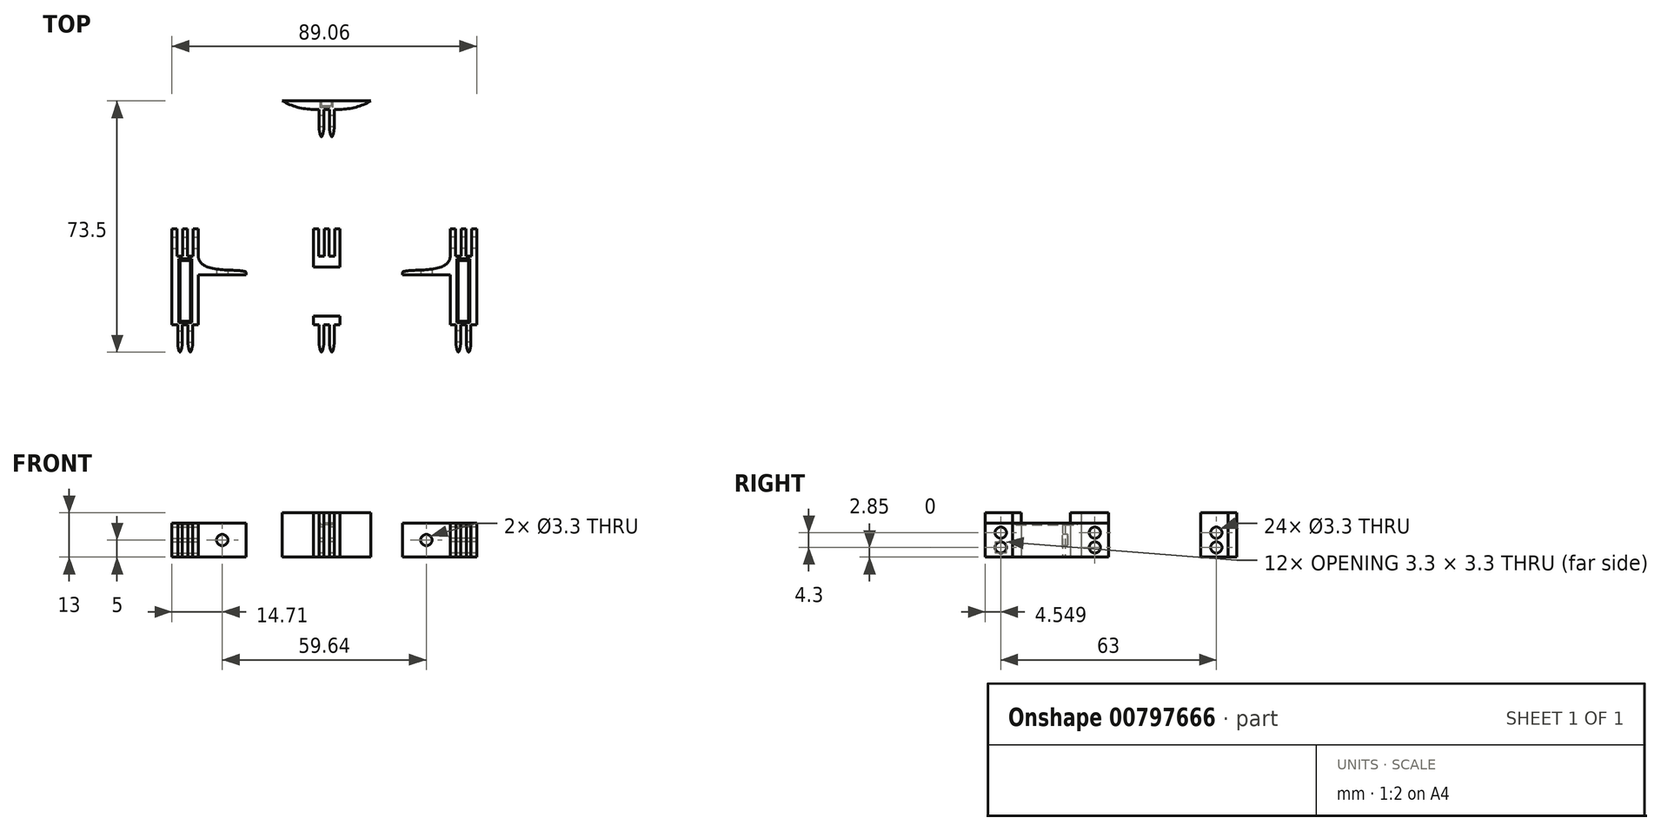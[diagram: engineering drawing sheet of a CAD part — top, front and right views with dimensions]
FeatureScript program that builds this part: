
annotation { "Feature Type Name" : "Feature", "Feature Type Description" : "" }
export const myFeature = defineFeature(function(context is Context, id is Id, definition is map)
    precondition{}
    {
        {
            var Q0;
            Q0=qCreatedBy(makeId("Top.planeOp"),FACE);
            var sketch = newSketch(context, id + "F0", { "sketchPlane" : qUnion([Q0])});
            skLineSegment(sketch, "E0", {"start": v(-17.18, 0) * mm, "end": v(-3.18, 0) * mm});
            skLineSegment(sketch, "E1", {"start": v(-3.18, 0) * mm, "end": v(-3.18, 11.16) * mm});
            skLineSegment(sketch, "E2", {"start": v(4.53, 11.16) * mm, "end": v(4.53, -16.94) * mm});
            skLineSegment(sketch, "E3", {"start": v(-17.18, 0) * mm, "end": v(-17.18, -2.3) * mm});
            skLineSegment(sketch, "E4", {"start": v(-17.18, -2.3) * mm, "end": v(-3.18, -2.3) * mm});
            skLineSegment(sketch, "E5", {"start": v(-3.18, -2.3) * mm, "end": v(-3.18, -16.94) * mm});
            skLineSegment(sketch, "E6", {"start": v(-3.18, 11.16) * mm, "end": v(-1.68, 11.16) * mm});
            skLineSegment(sketch, "E7", {"start": v(3.03, 11.16) * mm, "end": v(4.53, 11.16) * mm});
            skLineSegment(sketch, "E8", {"start": v(-1.68, 11.16) * mm, "end": v(-1.68, 3.06) * mm});
            skLineSegment(sketch, "E9", {"start": v(-1.68, 3.06) * mm, "end": v(0, 3.06) * mm});
            skLineSegment(sketch, "E10", {"start": v(0, 3.06) * mm, "end": v(0, 11.16) * mm});
            skLineSegment(sketch, "E11", {"start": v(0, 11.16) * mm, "end": v(1.35, 11.16) * mm});
            skLineSegment(sketch, "E12", {"start": v(1.35, 11.16) * mm, "end": v(1.35, 3.06) * mm});
            skLineSegment(sketch, "E13", {"start": v(1.35, 3.06) * mm, "end": v(3.03, 3.06) * mm});
            skLineSegment(sketch, "E14", {"start": v(3.03, 3.06) * mm, "end": v(3.03, 11.16) * mm});
            skLineSegment(sketch, "E15", {"start": v(4.53, -16.94) * mm, "end": v(2.86, -16.94) * mm});
            skLineSegment(sketch, "E16", {"start": v(2.86, -16.94) * mm, "end": v(2.86, -24.94) * mm});
            skLineSegment(sketch, "E17", {"start": v(2.86, -24.94) * mm, "end": v(1.51, -24.94) * mm});
            skLineSegment(sketch, "E18", {"start": v(1.52, -24.94) * mm, "end": v(1.52, -16.94) * mm});
            skLineSegment(sketch, "E19", {"start": v(1.51, -16.94) * mm, "end": v(-0.17, -16.94) * mm});
            skLineSegment(sketch, "E20", {"start": v(-0.17, -16.94) * mm, "end": v(-0.17, -24.94) * mm});
            skLineSegment(sketch, "E21", {"start": v(-0.17, -24.94) * mm, "end": v(-1.51, -24.94) * mm});
            skLineSegment(sketch, "E22", {"start": v(-1.51, -24.94) * mm, "end": v(-1.51, -16.94) * mm});
            skLineSegment(sketch, "E23", {"start": v(-1.51, -16.94) * mm, "end": v(-3.18, -16.94) * mm});
            skPoint(sketch, "E24", {"position": v(-10.18, -2.3) * mm});
            skLineSegment(sketch, "E25", {"start": v(-3.18, -14.44) * mm, "end": v(4.53, -14.44) * mm});
            skLineSegment(sketch, "E26", {"start": v(4.53, -14.44) * mm, "end": v(13.62, -14.44) * mm});
            skArc(sketch, "E27", {"start": v(4.53, -16.94) * mm, "mid": v(9.24, -16.28) * mm, "end": v(13.62, -14.44) * mm});
            skPoint(sketch, "E28", {"position": v(0.67, -14.44) * mm});
            skLineSegment(sketch, "E29", {"start": v(0.67, -14.44) * mm, "end": v(0.67, -16.3) * mm, "construction": true});
            skLineSegment(sketch, "E30.MirrorCS", {"start": v(-3.18, -14.44) * mm, "end": v(-12.27, -14.44) * mm});
            skArc(sketch, "E31.MirrorCS", {"start": v(-3.18, -16.94) * mm, "mid": v(-7.89, -16.28) * mm, "end": v(-12.27, -14.44) * mm});
            skLineSegment(sketch, "E32", {"start": v(-17.18, -2.3) * mm, "end": v(-17.18, -1.53) * mm});
            skFitSpline(sketch, "E33", {"points": [v(-17.18, -1.53) * mm, v(-3.18, 3.24) * mm], "startDerivative": vector(5.77, 3.68) * mm, "endDerivative": vector(0, 16.63) * mm});
            skLineSegment(sketch, "E34", {"start": v(-1.98, -16.94) * mm, "end": v(-1.98, -19.6) * mm, "construction": true});
            skLineSegment(sketch, "E35", {"start": v(-1.98, -19.6) * mm, "end": v(-1.98, -22.27) * mm, "construction": true});
            skLineSegment(sketch, "E36", {"start": v(-1.98, -22.27) * mm, "end": v(-1.98, -24.94) * mm, "construction": true});
            skPoint(sketch, "E37", {"position": v(-1.51, -22.44) * mm});
            skPoint(sketch, "E38", {"position": v(-0.17, -22.44) * mm});
            skFitSpline(sketch, "E39", {"points": [v(-1.51, -22.44) * mm, v(-0.84, -24.94) * mm, v(-0.17, -22.44) * mm], "startDerivative": vector(0, -3.73) * mm, "endDerivative": vector(0, 3.73) * mm});
            skLineSegment(sketch, "E40", {"start": v(0.67, -16.94) * mm, "end": v(0.67, -25.95) * mm, "construction": true});
            skFitSpline(sketch, "E41.MirrorCS", {"points": [v(2.86, -22.44) * mm, v(2.19, -24.94) * mm, v(1.52, -22.44) * mm], "startDerivative": vector(0, -3.73) * mm, "endDerivative": vector(0, 3.73) * mm});
            skLineSegment(sketch, "E42", {"start": v(-3.18, 0) * mm, "end": v(4.53, 0) * mm});
            skSolve(sketch);
        }
        {
            var Q0;
            {var subQ0=sQuery(id+"F0.wireOp",EDGE,"E0");Q0=makeQuery(id+"F0.imprint","IMPRINT",FACE,{"disambiguationData":[TD([[makeQuery(id+"F0.imprint","IMPRINT",EDGE,{"derivedFrom":subQ0}),1.0]])]});}
            var Q1;
            {var subQ7=sQuery(id+"F0.wireOp",EDGE,"E4");Q1=makeQuery(id+"F0.imprint","IMPRINT",FACE,{"disambiguationData":[TD([[makeQuery(id+"F0.imprint","IMPRINT",EDGE,{"derivedFrom":subQ7}),1.0]])]});}
            var Q2;
            {var subQ0=sQuery(id+"F0.wireOp",EDGE,"E15");Q2=makeQuery(id+"F0.imprint","IMPRINT",FACE,{"disambiguationData":[TD([[makeQuery(id+"F0.imprint","IMPRINT",EDGE,{"derivedFrom":subQ0}),-1.0]])]});}
            var Q3;
            {var subQ4=sQuery(id+"F0.wireOp",EDGE,"E6");Q3=makeQuery(id+"F0.imprint","IMPRINT",FACE,{"disambiguationData":[TD([[makeQuery(id+"F0.imprint","IMPRINT",EDGE,{"derivedFrom":subQ4}),-1.0]])]});}
            extrude(context, id + "F1", {"entities" : qUnion([Q0, Q1, Q2, Q3]), "depth" : 10 * mm, "offsetDistance" : 25 * mm});
        }
        {
            var Q0;
            {var subQ2=sQuery(id+"F0.wireOp",EDGE,"E30.MirrorCS");Q0=makeQuery(id+"F0.imprint","IMPRINT",FACE,{"disambiguationData":[TD([[makeQuery(id+"F0.imprint","IMPRINT",EDGE,{"derivedFrom":subQ2}),1.0]])]});}
            var Q1;
            {var subQ0=sQuery(id+"F0.wireOp",EDGE,"E15");Q1=makeQuery(id+"F0.imprint","IMPRINT",FACE,{"disambiguationData":[TD([[makeQuery(id+"F0.imprint","IMPRINT",EDGE,{"derivedFrom":subQ0}),-1.0]])]});}
            var Q2;
            {var subQ2=sQuery(id+"F0.wireOp",EDGE,"E26");Q2=makeQuery(id+"F0.imprint","IMPRINT",FACE,{"disambiguationData":[TD([[makeQuery(id+"F0.imprint","IMPRINT",EDGE,{"derivedFrom":subQ2}),-1.0]])]});}
            extrude(context, id + "F2", {"entities" : qUnion([Q0, Q1, Q2]), "depth" : 13 * mm, "offsetDistance" : 25 * mm});
        }
        {
            var Q0;
            Q0=makeQuery(id+"F1.opExtrude","SWEPT_FACE",FACE,{"disambiguationData":[OSD([sQuery(id+"F0.wireOp",EDGE,"E4")])]});
            var sketch = newSketch(context, id + "F3", { "sketchPlane" : qUnion([Q0])});
            skLineSegment(sketch, "E43.0", {"start": v(-17.18, 0) * mm, "end": v(-3.18, 0) * mm});
            skLineSegment(sketch, "E44.0", {"start": v(-17.18, 10) * mm, "end": v(-3.18, 10) * mm});
            skLineSegment(sketch, "E45", {"start": v(-3.18, 10) * mm, "end": v(-17.18, 0) * mm});
            skLineSegment(sketch, "E46", {"start": v(-17.18, 10) * mm, "end": v(-3.18, 0) * mm});
            skPoint(sketch, "E47", {"position": v(-10.18, 5) * mm});
            skSolve(sketch);
        }
        {
            var Q0;
            Q0=sQuery(id+"F3.wireOp",VERTEX,"E47");
            var Q1;
            Q1=makeQuery(id+"F1.opExtrude","SWEPT_BODY",BODY,{"disambiguationData":[OSD([sQuery(id+"F0.wireOp",EDGE,"E0"),sQuery(id+"F0.wireOp",EDGE,"E1"),sQuery(id+"F0.wireOp",EDGE,"E2"),sQuery(id+"F0.wireOp",EDGE,"E3"),sQuery(id+"F0.wireOp",EDGE,"E4"),sQuery(id+"F0.wireOp",EDGE,"E5"),sQuery(id+"F0.wireOp",EDGE,"E6"),sQuery(id+"F0.wireOp",EDGE,"E7"),sQuery(id+"F0.wireOp",EDGE,"E8"),sQuery(id+"F0.wireOp",EDGE,"E9"),sQuery(id+"F0.wireOp",EDGE,"E10"),sQuery(id+"F0.wireOp",EDGE,"E11"),sQuery(id+"F0.wireOp",EDGE,"E12"),sQuery(id+"F0.wireOp",EDGE,"E13"),sQuery(id+"F0.wireOp",EDGE,"E14"),sQuery(id+"F0.wireOp",EDGE,"E15"),sQuery(id+"F0.wireOp",EDGE,"E16"),sQuery(id+"F0.wireOp",EDGE,"E17"),sQuery(id+"F0.wireOp",EDGE,"E18"),sQuery(id+"F0.wireOp",EDGE,"E19"),sQuery(id+"F0.wireOp",EDGE,"E20"),sQuery(id+"F0.wireOp",EDGE,"E21"),sQuery(id+"F0.wireOp",EDGE,"E22"),sQuery(id+"F0.wireOp",EDGE,"E23")])]});
            hole(context, id + "F4", {"style" : HoleStyle.SIMPLE, "endStyle" : HoleEndStyle.THROUGH, "standardTappedOrClearance" : lookupTablePath({ "standard" : "ISO", "fit" : "Normal", "size" : "M3", "type" : "Clearance" }), "standardBlindInLast" : lookupTablePath({ "fit" : "Standard", "standard" : "ISO", "size" : "M3", "type" : "Clearance" }), "holeDiameter" : 3.3 * mm, "majorDiameter" : 3 * mm, "isTappedThrough" : true, "tappedDepth" : 12 * mm, "tapClearance" : 3, "locations" : qUnion([Q0]), "scope" : qUnion([Q1])});
        }
        {
            var Q0;
            Q0=makeQuery(id+"F1.opExtrude","SWEPT_FACE",FACE,{"disambiguationData":[OSD([sQuery(id+"F0.wireOp",EDGE,"E5")])]});
            var sketch = newSketch(context, id + "F5", { "sketchPlane" : qUnion([Q0])});
            skLineSegment(sketch, "E48.0", {"start": v(2.3, 10) * mm, "end": v(16.94, 10) * mm});
            skPoint(sketch, "E49.0", {"position": v(9.62, 0) * mm});
            skLineSegment(sketch, "E50", {"start": v(9.62, 0) * mm, "end": v(9.62, 10) * mm});
            skPoint(sketch, "E51", {"position": v(9.62, 5) * mm});
            skSolve(sketch);
        }
        {
            var Q0;
            Q0=makeQuery(id+"F1.opExtrude","SWEPT_FACE",FACE,{"disambiguationData":[OSD([sQuery(id+"F0.wireOp",EDGE,"E1")])]});
            var sketch = newSketch(context, id + "F6", { "sketchPlane" : qUnion([Q0])});
            skPoint(sketch, "E52.0", {"position": v(-7.1, 10) * mm});
            skPoint(sketch, "E53", {"position": v(-6.6, 7.15) * mm});
            skPoint(sketch, "E54", {"position": v(-6.6, 2.85) * mm});
            skPoint(sketch, "E55", {"position": v(-7.1, 2.85) * mm});
            skPoint(sketch, "E56", {"position": v(-7.1, 7.15) * mm});
            skFitSpline(sketch, "E57.0.0", {"points": [v(22.44, 0) * mm, v(23.27, 0) * mm, v(24.1, 0) * mm, v(24.94, 0) * mm]});
            skLineSegment(sketch, "E57.0.1", {"start": v(22.44, 0) * mm, "end": v(22.44, 10) * mm});
            skFitSpline(sketch, "E57.0.2", {"points": [v(22.44, 10) * mm, v(23.27, 10) * mm, v(24.1, 10) * mm, v(24.94, 10) * mm]});
            skLineSegment(sketch, "E58.0.0", {"start": v(16.94, 0) * mm, "end": v(22.44, 0) * mm});
            skLineSegment(sketch, "E58.0.2", {"start": v(22.44, 10) * mm, "end": v(16.94, 10) * mm});
            skLineSegment(sketch, "E58.0.3", {"start": v(16.94, 10) * mm, "end": v(16.94, 0) * mm});
            skLineSegment(sketch, "E59", {"start": v(-7.1, 7.15) * mm, "end": v(-8.14, 7.15) * mm, "construction": true});
            skLineSegment(sketch, "E60", {"start": v(-6.6, 5) * mm, "end": v(-11.16, 5) * mm, "construction": true});
            skLineSegment(sketch, "E61", {"start": v(24.94, 0) * mm, "end": v(24.94, 10) * mm});
            skLineSegment(sketch, "E62", {"start": v(24.94, 7.97) * mm, "end": v(20.4, 7.97) * mm, "construction": true});
            skLineSegment(sketch, "E63", {"start": v(20.4, 10) * mm, "end": v(20.4, 0) * mm});
            skLineSegment(sketch, "E64", {"start": v(-6.6, 2.85) * mm, "end": v(20.4, 2.85) * mm, "construction": true});
            skLineSegment(sketch, "E65", {"start": v(-6.6, 7.15) * mm, "end": v(20.4, 7.15) * mm, "construction": true});
            skLineSegment(sketch, "E66", {"start": v(-6.6, 2.85) * mm, "end": v(-6.6, 5) * mm});
            skLineSegment(sketch, "E67", {"start": v(-6.6, 7.15) * mm, "end": v(-6.6, 5) * mm});
            skSolve(sketch);
        }
        {
            var Q0;
            Q0=makeQuery(id+"F1.opExtrude","SWEPT_FACE",FACE,{"disambiguationData":[OSD([sQuery(id+"F0.wireOp",EDGE,"E22")])]});
            var sketch = newSketch(context, id + "F7", { "sketchPlane" : qUnion([Q0])});
            skSolve(sketch);
        }
        {
            var Q0;
            Q0=sQuery(id+"F7.wireOp",VERTEX,"cb130fc7-3e3b-43d1-b807-29a7db9d23ac");
            var Q1;
            Q1=sQuery(id+"F7.wireOp",VERTEX,"a07335c5-b8a1-44e3-ba5a-ccb4c6ddec3e");
            var Q2;
            Q2=sQuery(id+"F6.wireOp",VERTEX,"E56");
            var Q3;
            Q3=sQuery(id+"F6.wireOp",VERTEX,"E55");
            var Q4;
            Q4=sQuery(id+"F6.wireOp",VERTEX,"HQiPWZDy-e3eu-RUYi-kAzC-jWAaY2hU2Ehy.end");
            var Q5;
            Q5=sQuery(id+"F6.wireOp",VERTEX,"tANYXxDx-TpeI-LTaA-ofTa-CKFf57kc3H1u.end");
            var Q6;
            Q6=sQuery(id+"F6.wireOp",VERTEX,"E65.end");
            var Q7;
            Q7=sQuery(id+"F6.wireOp",VERTEX,"E64.end");
            var Q8;
            Q8=makeQuery(id+"F1.opExtrude","SWEPT_BODY",BODY,{"disambiguationData":[OSD([sQuery(id+"F0.wireOp",EDGE,"E0"),sQuery(id+"F0.wireOp",EDGE,"E1"),sQuery(id+"F0.wireOp",EDGE,"E2"),sQuery(id+"F0.wireOp",EDGE,"E3"),sQuery(id+"F0.wireOp",EDGE,"E4"),sQuery(id+"F0.wireOp",EDGE,"E5"),sQuery(id+"F0.wireOp",EDGE,"E6"),sQuery(id+"F0.wireOp",EDGE,"E7"),sQuery(id+"F0.wireOp",EDGE,"E8"),sQuery(id+"F0.wireOp",EDGE,"E9"),sQuery(id+"F0.wireOp",EDGE,"E10"),sQuery(id+"F0.wireOp",EDGE,"E11"),sQuery(id+"F0.wireOp",EDGE,"E12"),sQuery(id+"F0.wireOp",EDGE,"E13"),sQuery(id+"F0.wireOp",EDGE,"E14"),sQuery(id+"F0.wireOp",EDGE,"E15"),sQuery(id+"F0.wireOp",EDGE,"E16"),sQuery(id+"F0.wireOp",EDGE,"E17"),sQuery(id+"F0.wireOp",EDGE,"E18"),sQuery(id+"F0.wireOp",EDGE,"E19"),sQuery(id+"F0.wireOp",EDGE,"E20"),sQuery(id+"F0.wireOp",EDGE,"E21"),sQuery(id+"F0.wireOp",EDGE,"E22"),sQuery(id+"F0.wireOp",EDGE,"E23")])]});
            var Q9;
            Q9=makeQuery(id+"F2.opExtrude","SWEPT_BODY",BODY,{"disambiguationData":[OSD([sQuery(id+"F0.wireOp",EDGE,"E15"),sQuery(id+"F0.wireOp",EDGE,"E16"),sQuery(id+"F0.wireOp",EDGE,"E17"),sQuery(id+"F0.wireOp",EDGE,"E18"),sQuery(id+"F0.wireOp",EDGE,"E19"),sQuery(id+"F0.wireOp",EDGE,"E20"),sQuery(id+"F0.wireOp",EDGE,"E21"),sQuery(id+"F0.wireOp",EDGE,"E22"),sQuery(id+"F0.wireOp",EDGE,"E23"),sQuery(id+"F0.wireOp",EDGE,"E25"),sQuery(id+"F0.wireOp",EDGE,"E26"),sQuery(id+"F0.wireOp",EDGE,"E27"),sQuery(id+"F0.wireOp",EDGE,"E30.MirrorCS"),sQuery(id+"F0.wireOp",EDGE,"E31.MirrorCS")])]});
            hole(context, id + "F8", {"style" : HoleStyle.SIMPLE, "endStyle" : HoleEndStyle.THROUGH, "standardTappedOrClearance" : lookupTablePath({ "standard" : "ISO", "fit" : "Normal", "size" : "M3", "type" : "Clearance" }), "standardBlindInLast" : lookupTablePath({ "fit" : "Standard", "standard" : "ISO", "size" : "M3", "type" : "Clearance" }), "holeDiameter" : 3.3 * mm, "majorDiameter" : 5 * mm, "isTappedThrough" : true, "tappedDepth" : 12 * mm, "tapClearance" : 3, "locations" : qUnion([Q0, Q1, Q2, Q3, Q4, Q5, Q6, Q7]), "scope" : qUnion([Q8, Q9])});
        }
        {
            var Q0;
            Q0=makeQuery(id+"F1.opExtrude","CAP_FACE",FACE,{"disambiguationData":[OSD([sQuery(id+"F0.wireOp",EDGE,"E0"),sQuery(id+"F0.wireOp",EDGE,"E1"),sQuery(id+"F0.wireOp",EDGE,"E2"),sQuery(id+"F0.wireOp",EDGE,"E3"),sQuery(id+"F0.wireOp",EDGE,"E4"),sQuery(id+"F0.wireOp",EDGE,"E5"),sQuery(id+"F0.wireOp",EDGE,"E6"),sQuery(id+"F0.wireOp",EDGE,"E7"),sQuery(id+"F0.wireOp",EDGE,"E8"),sQuery(id+"F0.wireOp",EDGE,"E9"),sQuery(id+"F0.wireOp",EDGE,"E10"),sQuery(id+"F0.wireOp",EDGE,"E11"),sQuery(id+"F0.wireOp",EDGE,"E12"),sQuery(id+"F0.wireOp",EDGE,"E13"),sQuery(id+"F0.wireOp",EDGE,"E14"),sQuery(id+"F0.wireOp",EDGE,"E15"),sQuery(id+"F0.wireOp",EDGE,"E16"),sQuery(id+"F0.wireOp",EDGE,"E17"),sQuery(id+"F0.wireOp",EDGE,"E18"),sQuery(id+"F0.wireOp",EDGE,"E19"),sQuery(id+"F0.wireOp",EDGE,"E20"),sQuery(id+"F0.wireOp",EDGE,"E21"),sQuery(id+"F0.wireOp",EDGE,"E22"),sQuery(id+"F0.wireOp",EDGE,"E23")])],"isStart":false});
            var sketch = newSketch(context, id + "F9", { "sketchPlane" : qUnion([Q0])});
            skLineSegment(sketch, "E68.bottom", {"start": v(3.3, -17.04) * mm, "end": v(-2, -17.04) * mm});
            skLineSegment(sketch, "E68.top", {"start": v(3.3, 3.06) * mm, "end": v(-2, 3.06) * mm});
            skLineSegment(sketch, "E68.left", {"start": v(3.3, -17.04) * mm, "end": v(3.3, 3.06) * mm});
            skLineSegment(sketch, "E68.right", {"start": v(-2, -17.04) * mm, "end": v(-2, 3.06) * mm});
            skLineSegment(sketch, "E69.0", {"start": v(2.55, -16.3) * mm, "end": v(-1.25, -16.3) * mm});
            skLineSegment(sketch, "E69.1", {"start": v(2.55, -16.3) * mm, "end": v(2.55, 2.3) * mm});
            skLineSegment(sketch, "E69.2", {"start": v(2.55, 2.3) * mm, "end": v(-1.25, 2.3) * mm});
            skLineSegment(sketch, "E69.3", {"start": v(-1.25, -16.3) * mm, "end": v(-1.25, 2.3) * mm});
            skLineSegment(sketch, "E70", {"start": v(-2, -1.3) * mm, "end": v(-1.25, -1.3) * mm});
            skLineSegment(sketch, "E71", {"start": v(0.65, -16.3) * mm, "end": v(0.65, -14.4) * mm});
            skLineSegment(sketch, "E72", {"start": v(2.55, -14.4) * mm, "end": v(0.65, -14.4) * mm});
            skLineSegment(sketch, "E73", {"start": v(-1.25, -14.4) * mm, "end": v(0.65, -14.4) * mm});
            skLineSegment(sketch, "E74", {"start": v(0.65, -14.4) * mm, "end": v(0.65, -12.5) * mm});
            skLineSegment(sketch, "E75", {"start": v(0.65, -12.5) * mm, "end": v(0.65, -10.6) * mm});
            skLineSegment(sketch, "E76", {"start": v(0.65, -10.6) * mm, "end": v(0.65, -8.7) * mm});
            skLineSegment(sketch, "E77", {"start": v(0.65, -8.7) * mm, "end": v(0.65, -6.8) * mm});
            skLineSegment(sketch, "E78", {"start": v(0.65, -6.8) * mm, "end": v(0.65, -4.9) * mm});
            skLineSegment(sketch, "E79", {"start": v(0.65, -12.5) * mm, "end": v(2.55, -12.5) * mm});
            skLineSegment(sketch, "E80", {"start": v(0.65, -12.5) * mm, "end": v(-1.25, -12.5) * mm});
            skLineSegment(sketch, "E81", {"start": v(0.65, -10.6) * mm, "end": v(-1.25, -10.6) * mm});
            skLineSegment(sketch, "E82", {"start": v(0.65, -8.7) * mm, "end": v(-1.25, -8.7) * mm});
            skLineSegment(sketch, "E83", {"start": v(0.65, -6.8) * mm, "end": v(-1.25, -6.8) * mm});
            skLineSegment(sketch, "E84", {"start": v(0.65, -6.8) * mm, "end": v(2.55, -6.8) * mm});
            skLineSegment(sketch, "E85", {"start": v(0.65, -8.7) * mm, "end": v(2.55, -8.7) * mm});
            skLineSegment(sketch, "E86", {"start": v(0.65, -10.6) * mm, "end": v(2.55, -10.6) * mm});
            skLineSegment(sketch, "E87", {"start": v(0.65, -4.9) * mm, "end": v(2.55, -4.9) * mm});
            skLineSegment(sketch, "E88", {"start": v(0.65, -4.9) * mm, "end": v(-1.25, -4.9) * mm});
            skLineSegment(sketch, "E89", {"start": v(0.65, -4.9) * mm, "end": v(0.65, -3) * mm});
            skLineSegment(sketch, "E90", {"start": v(0.65, -3) * mm, "end": v(0.65, -1.1) * mm});
            skLineSegment(sketch, "E91", {"start": v(0.65, -1.1) * mm, "end": v(2.55, -1.1) * mm});
            skLineSegment(sketch, "E92", {"start": v(0.65, -1.1) * mm, "end": v(-1.25, -1.1) * mm});
            skLineSegment(sketch, "E93", {"start": v(0.65, -3) * mm, "end": v(-1.25, -3) * mm});
            skLineSegment(sketch, "E94", {"start": v(0.65, -3) * mm, "end": v(2.55, -3) * mm});
            skSolve(sketch);
        }
        {
            var Q0;
            {var subQ3=sQuery(id+"F9.wireOp",EDGE,"E71");Q0=makeQuery(id+"F9.imprint","IMPRINT",FACE,{"disambiguationData":[TD([[makeQuery(id+"F9.imprint","IMPRINT",EDGE,{"derivedFrom":subQ3}),1.0]])]});}
            var Q1;
            {var subQ0=sQuery(id+"F9.wireOp",EDGE,"E72");Q1=makeQuery(id+"F9.imprint","IMPRINT",FACE,{"disambiguationData":[TD([[makeQuery(id+"F9.imprint","IMPRINT",EDGE,{"derivedFrom":subQ0}),-1.0]])]});}
            var Q2;
            Q2=makeQuery(id+"F9.imprint","IMPRINT",FACE,{"disambiguationData":[TD([[makeQuery(id+"F9.imprint","IMPRINT",EDGE,{"derivedFrom":sQuery(id+"F9.wireOp",EDGE,"E75")}),1.0]])]});
            var Q3;
            Q3=makeQuery(id+"F9.imprint","IMPRINT",FACE,{"disambiguationData":[TD([[makeQuery(id+"F9.imprint","IMPRINT",EDGE,{"derivedFrom":sQuery(id+"F9.wireOp",EDGE,"E76")}),-1.0]])]});
            var Q4;
            Q4=makeQuery(id+"F9.imprint","IMPRINT",FACE,{"disambiguationData":[TD([[makeQuery(id+"F9.imprint","IMPRINT",EDGE,{"derivedFrom":sQuery(id+"F9.wireOp",EDGE,"E77")}),1.0]])]});
            var Q5;
            Q5=makeQuery(id+"F9.imprint","IMPRINT",FACE,{"disambiguationData":[TD([[makeQuery(id+"F9.imprint","IMPRINT",EDGE,{"derivedFrom":sQuery(id+"F9.wireOp",EDGE,"E78")}),-1.0]])]});
            var Q6;
            {var subQ0=sQuery(id+"F9.wireOp",EDGE,"E88");Q6=makeQuery(id+"F9.imprint","IMPRINT",FACE,{"disambiguationData":[TD([[makeQuery(id+"F9.imprint","IMPRINT",EDGE,{"derivedFrom":subQ0}),-1.0]])]});}
            var Q7;
            Q7=makeQuery(id+"F9.imprint","IMPRINT",FACE,{"disambiguationData":[TD([[makeQuery(id+"F9.imprint","IMPRINT",EDGE,{"derivedFrom":sQuery(id+"F9.wireOp",EDGE,"E90")}),-1.0]])]});
            var Q8;
            {var subQ3=sQuery(id+"F9.wireOp",EDGE,"E71");Q8=makeQuery(id+"F9.imprint","IMPRINT",FACE,{"disambiguationData":[TD([[makeQuery(id+"F9.imprint","IMPRINT",EDGE,{"derivedFrom":subQ3}),-1.0]])]});}
            var Q9;
            {var subQ0=sQuery(id+"F9.wireOp",EDGE,"E73");Q9=makeQuery(id+"F9.imprint","IMPRINT",FACE,{"disambiguationData":[TD([[makeQuery(id+"F9.imprint","IMPRINT",EDGE,{"derivedFrom":subQ0}),1.0]])]});}
            var Q10;
            Q10=makeQuery(id+"F9.imprint","IMPRINT",FACE,{"disambiguationData":[TD([[makeQuery(id+"F9.imprint","IMPRINT",EDGE,{"derivedFrom":sQuery(id+"F9.wireOp",EDGE,"E75")}),-1.0]])]});
            var Q11;
            Q11=makeQuery(id+"F9.imprint","IMPRINT",FACE,{"disambiguationData":[TD([[makeQuery(id+"F9.imprint","IMPRINT",EDGE,{"derivedFrom":sQuery(id+"F9.wireOp",EDGE,"E76")}),1.0]])]});
            var Q12;
            Q12=makeQuery(id+"F9.imprint","IMPRINT",FACE,{"disambiguationData":[TD([[makeQuery(id+"F9.imprint","IMPRINT",EDGE,{"derivedFrom":sQuery(id+"F9.wireOp",EDGE,"E77")}),-1.0]])]});
            var Q13;
            Q13=makeQuery(id+"F9.imprint","IMPRINT",FACE,{"disambiguationData":[TD([[makeQuery(id+"F9.imprint","IMPRINT",EDGE,{"derivedFrom":sQuery(id+"F9.wireOp",EDGE,"E78")}),1.0]])]});
            var Q14;
            {var subQ0=sQuery(id+"F9.wireOp",EDGE,"E87");Q14=makeQuery(id+"F9.imprint","IMPRINT",FACE,{"disambiguationData":[TD([[makeQuery(id+"F9.imprint","IMPRINT",EDGE,{"derivedFrom":subQ0}),1.0]])]});}
            var Q15;
            Q15=makeQuery(id+"F9.imprint","IMPRINT",FACE,{"disambiguationData":[TD([[makeQuery(id+"F9.imprint","IMPRINT",EDGE,{"derivedFrom":sQuery(id+"F9.wireOp",EDGE,"E90")}),1.0]])]});
            var Q16;
            {var subQ2=sQuery(id+"F9.wireOp",EDGE,"E69.2");Q16=makeQuery(id+"F9.imprint","IMPRINT",FACE,{"disambiguationData":[TD([[makeQuery(id+"F9.imprint","IMPRINT",EDGE,{"derivedFrom":subQ2}),1.0]])]});}
            extrude(context, id + "F10", {"entities" : qUnion([Q0, Q1, Q2, Q3, Q4, Q5, Q6, Q7, Q8, Q9, Q10, Q11, Q12, Q13, Q14, Q15, Q16]), "operationType" : NewBodyOperationType.REMOVE, "oppositeDirection" : true, "depth" : 0.5 * mm, "offsetDistance" : 25 * mm, "hasDraft" : true, "draftAngle" : 40 * degree, "draftPullDirection" : true});
        }
        {
            var Q0;
            Q0=makeQuery(id+"F1.opExtrude","SWEPT_BODY",BODY,{"disambiguationData":[OSD([sQuery(id+"F0.wireOp",EDGE,"E0"),sQuery(id+"F0.wireOp",EDGE,"E1"),sQuery(id+"F0.wireOp",EDGE,"E2"),sQuery(id+"F0.wireOp",EDGE,"E3"),sQuery(id+"F0.wireOp",EDGE,"E4"),sQuery(id+"F0.wireOp",EDGE,"E5"),sQuery(id+"F0.wireOp",EDGE,"E6"),sQuery(id+"F0.wireOp",EDGE,"E7"),sQuery(id+"F0.wireOp",EDGE,"E8"),sQuery(id+"F0.wireOp",EDGE,"E9"),sQuery(id+"F0.wireOp",EDGE,"E10"),sQuery(id+"F0.wireOp",EDGE,"E11"),sQuery(id+"F0.wireOp",EDGE,"E12"),sQuery(id+"F0.wireOp",EDGE,"E13"),sQuery(id+"F0.wireOp",EDGE,"E14"),sQuery(id+"F0.wireOp",EDGE,"E15"),sQuery(id+"F0.wireOp",EDGE,"E16"),sQuery(id+"F0.wireOp",EDGE,"E17"),sQuery(id+"F0.wireOp",EDGE,"E18"),sQuery(id+"F0.wireOp",EDGE,"E19"),sQuery(id+"F0.wireOp",EDGE,"E20"),sQuery(id+"F0.wireOp",EDGE,"E21"),sQuery(id+"F0.wireOp",EDGE,"E22"),sQuery(id+"F0.wireOp",EDGE,"E23")])]});
            transform(context, id + "F11", {"entities" : qUnion([Q0]), "transformType" : TransformType.TRANSLATION_3D, "dx" : 40 * mm, "dy" : 0 * mm, "dz" : 0 * mm, "makeCopy" : false});
        }
        {
            var Q0;
            Q0=makeQuery(id+"F1.opExtrude","SWEPT_BODY",BODY,{"disambiguationData":[OSD([sQuery(id+"F0.wireOp",EDGE,"E0"),sQuery(id+"F0.wireOp",EDGE,"E1"),sQuery(id+"F0.wireOp",EDGE,"E2"),sQuery(id+"F0.wireOp",EDGE,"E3"),sQuery(id+"F0.wireOp",EDGE,"E4"),sQuery(id+"F0.wireOp",EDGE,"E5"),sQuery(id+"F0.wireOp",EDGE,"E6"),sQuery(id+"F0.wireOp",EDGE,"E7"),sQuery(id+"F0.wireOp",EDGE,"E8"),sQuery(id+"F0.wireOp",EDGE,"E9"),sQuery(id+"F0.wireOp",EDGE,"E10"),sQuery(id+"F0.wireOp",EDGE,"E11"),sQuery(id+"F0.wireOp",EDGE,"E12"),sQuery(id+"F0.wireOp",EDGE,"E13"),sQuery(id+"F0.wireOp",EDGE,"E14"),sQuery(id+"F0.wireOp",EDGE,"E15"),sQuery(id+"F0.wireOp",EDGE,"E16"),sQuery(id+"F0.wireOp",EDGE,"E17"),sQuery(id+"F0.wireOp",EDGE,"E18"),sQuery(id+"F0.wireOp",EDGE,"E19"),sQuery(id+"F0.wireOp",EDGE,"E20"),sQuery(id+"F0.wireOp",EDGE,"E21"),sQuery(id+"F0.wireOp",EDGE,"E22"),sQuery(id+"F0.wireOp",EDGE,"E23")])]});
            var Q1;
            Q1=qCreatedBy(makeId("Right.planeOp"),FACE);
            mirror(context, id + "F12", {"entities" : qUnion([Q0]), "mirrorPlane" : qUnion([Q1])});
        }
        {
            var Q0;
            {var subQ12=sQuery(id+"F0.wireOp",EDGE,"E15");Q0=makeQuery(id+"F0.imprint","IMPRINT",FACE,{"disambiguationData":[TD([[makeQuery(id+"F0.imprint","IMPRINT",EDGE,{"derivedFrom":subQ12}),-1.0]])]});}
            var Q1;
            {var subQ4=sQuery(id+"F0.wireOp",EDGE,"E6");Q1=makeQuery(id+"F0.imprint","IMPRINT",FACE,{"disambiguationData":[TD([[makeQuery(id+"F0.imprint","IMPRINT",EDGE,{"derivedFrom":subQ4}),-1.0]])]});}
            extrude(context, id + "F13", {"entities" : qUnion([Q0, Q1]), "depth" : 13 * mm, "offsetDistance" : 25 * mm});
        }
        {
            var Q0;
            Q0=makeQuery(id+"F2.opExtrude","SWEPT_BODY",BODY,{"disambiguationData":[OSD([sQuery(id+"F0.wireOp",EDGE,"E15"),sQuery(id+"F0.wireOp",EDGE,"E16"),sQuery(id+"F0.wireOp",EDGE,"E17"),sQuery(id+"F0.wireOp",EDGE,"E18"),sQuery(id+"F0.wireOp",EDGE,"E19"),sQuery(id+"F0.wireOp",EDGE,"E20"),sQuery(id+"F0.wireOp",EDGE,"E21"),sQuery(id+"F0.wireOp",EDGE,"E22"),sQuery(id+"F0.wireOp",EDGE,"E23"),sQuery(id+"F0.wireOp",EDGE,"E25"),sQuery(id+"F0.wireOp",EDGE,"E26"),sQuery(id+"F0.wireOp",EDGE,"E27"),sQuery(id+"F0.wireOp",EDGE,"E30.MirrorCS"),sQuery(id+"F0.wireOp",EDGE,"E31.MirrorCS")])]});
            transform(context, id + "F14", {"entities" : qUnion([Q0]), "transformType" : TransformType.TRANSLATION_3D, "dx" : 0 * mm, "dy" : 63 * mm, "dz" : 0 * mm, "makeCopy" : false});
        }
    });
